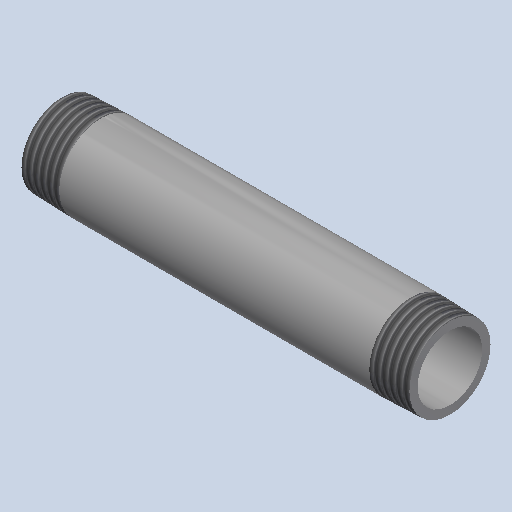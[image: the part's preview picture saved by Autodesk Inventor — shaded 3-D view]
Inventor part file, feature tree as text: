
AUTODESK INVENTOR PART (.ipt)
format: ipt  version: 2025 (Build 290162000, 162)  size: 212,480 bytes
history: native  units: mm (DEFAULTED — no unit token found)
features: other x8, revolve x1
ambient origin geometry x8: Origin, YZ Plane, XZ Plane, XY Plane, X Axis, Y Axis, Z Axis, Center Point
bodies: Solid1 (feature_tree)
feature tree (9):
  revolve  "Revolution1"  [1 undecoded]
  other  "Work Axis1"
  other  "Work Point5"
  other  "Work Axis2"
  other  "Work Point6"
  other  "Work Axis3"
  other  "Work Axis4"
  other  "Work Point7"
  other  "Work Point8"
note: 1 required parameter value undecoded (feature->parameter linkage not recoverable at this tier; creation-order binding heuristic only, values carry confidence <= 0.55)
